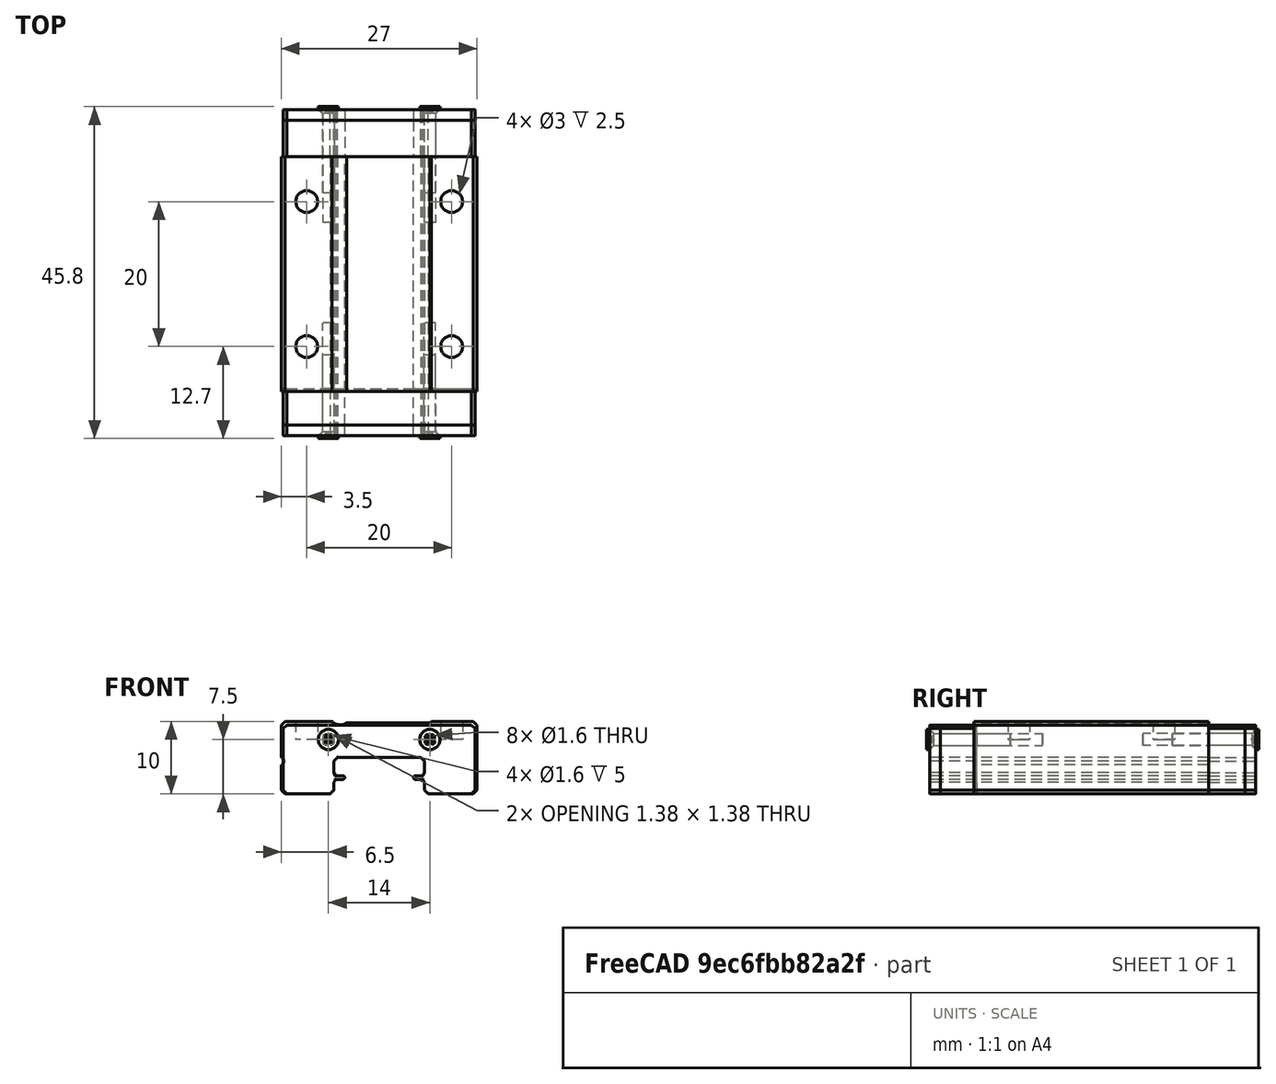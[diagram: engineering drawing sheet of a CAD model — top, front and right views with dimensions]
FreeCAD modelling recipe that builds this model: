
FCSTD DOCUMENT  (FreeCAD 0.19R24267 (Git))
Label: mgn12h-block
License: All rights reserved
LicenseURL: http://en.wikipedia.org/wiki/All_rights_reserved
objects: Part::Feature×9, Part::Compound×3
note: 12 computed .brp shape members not serialized (recipe doc carries the construction recipe); baked Part::Feature solids carry a one-line shape summary decoded from their .brp

FEATURE [Part::Feature] Body001  label="MGN 12H Lagerbock-Körper"
  shape: bbox 27 x 32.4 x 10 mm, 53 faces (baked)
FEATURE [Part::Feature] Body002  label="MGN 12H Lagerbock-Kugellager-Deckscheibe"
  Placement = pos=(0,10,0) rot=(0,0,1;0rad)
  shape: bbox 26.5 x 1.5 x 9.5 mm, 62 faces (baked)
FEATURE [Part::Feature] Body003  label="MGN 12H Lagerbock-Kugellager-Sperre"
  Placement = pos=(0,15,0) rot=(0,0,1;0rad)
  shape: bbox 26.5 x 5 x 9.5 mm, 32 faces (baked)
FEATURE [Part::Compound] Compound  label="MGN 12H Endstueck01"
  Links = -> [Body003,Body002]
  Placement = pos=(0,-47,0) rot=(0,0,1;0rad)
FEATURE [Part::Feature] Body004  label="MGN 12H Lagerbock-Kugellager-Sperre001"
  Placement = pos=(0,15,0) rot=(0,0,1;0rad)
  shape: bbox 26.5 x 5 x 9.5 mm, 32 faces (baked)
FEATURE [Part::Feature] Body005  label="MGN 12H Lagerbock-Kugellager-Deckscheibe001"
  Placement = pos=(0,10,0) rot=(0,0,1;0rad)
  shape: bbox 26.5 x 1.5 x 9.5 mm, 62 faces (baked)
FEATURE [Part::Compound] Compound001  label="MGN 12H Endstueck02"
  Links = -> [Body004,Body005]
  Placement = pos=(-12,15,0) rot=(0,0,1;3.14159rad)
FEATURE [Part::Feature] Screw002  label="M1.6x16-Screw001"
  Placement = pos=(1,6.9,10.5) rot=(-1,0,0;1.5708rad)
  shape: bbox 2.8 x 16 x 2.8 mm, 27 faces (baked)
FEATURE [Part::Feature] Screw003  label="M1.6x16-Screw002"
  Placement = pos=(-13,6.9,10.5) rot=(-1,0,0;1.5708rad)
  shape: bbox 2.8 x 16 x 2.8 mm, 27 faces (baked)
FEATURE [Part::Feature] Screw004  label="M1.6x16-Screw003"
  Placement = pos=(1,-38.9,10.5) rot=(1,0,0;1.5708rad)
  shape: bbox 2.8 x 16 x 2.8 mm, 27 faces (baked)
FEATURE [Part::Feature] Screw005  label="M1.6x16-Screw004"
  Placement = pos=(-13,-38.9,10.5) rot=(1,0,0;1.5708rad)
  shape: bbox 2.8 x 16 x 2.8 mm, 27 faces (baked)
FEATURE [Part::Compound] Compound002  label="MGN 12H Lagerbock"
  Links = -> [Body001,Compound,Compound001,Screw002,Screw003,Screw005,Screw004]
